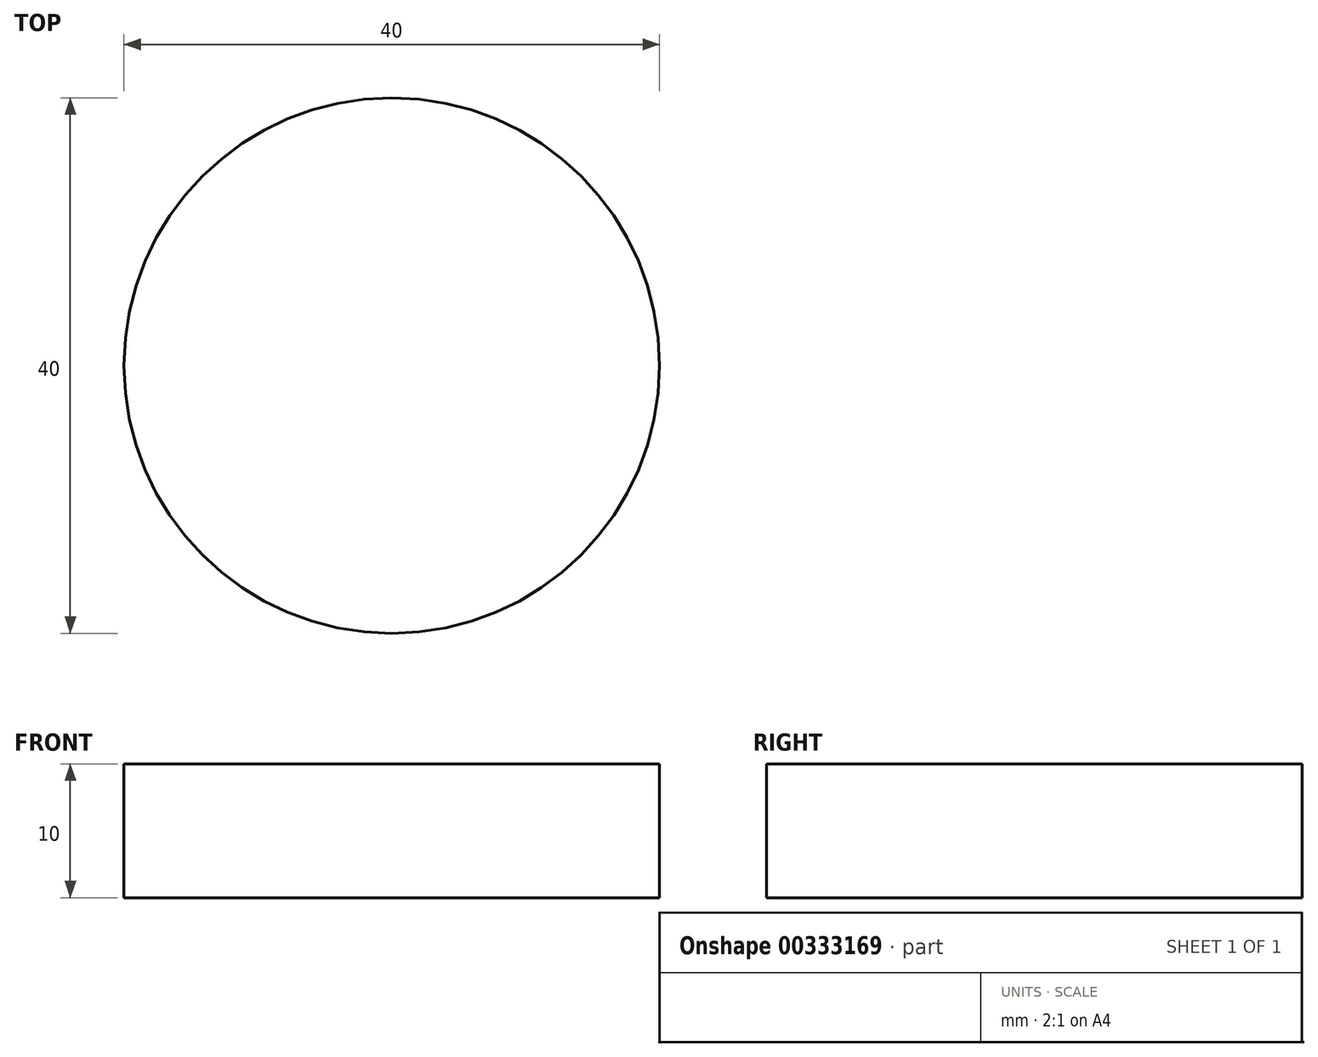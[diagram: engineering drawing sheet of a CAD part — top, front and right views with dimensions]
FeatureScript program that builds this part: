
annotation { "Feature Type Name" : "Feature", "Feature Type Description" : "" }
export const myFeature = defineFeature(function(context is Context, id is Id, definition is map)
    precondition{}
    {
        {
            var Q0;
            Q0=qCreatedBy(makeId("Top.planeOp"),FACE);
            var sketch = newSketch(context, id + "F0", { "sketchPlane" : qUnion([Q0])});
            skCircle(sketch, "E0", {"center": v(0, 0) * mm, "radius": 20 * mm});
            skSolve(sketch);
        }
        {
            var Q0;
            Q0=qSketchRegion(id+"F0",true);
            extrude(context, id + "F1", {"entities" : qUnion([Q0]), "depth" : 10 * mm});
        }
    });
